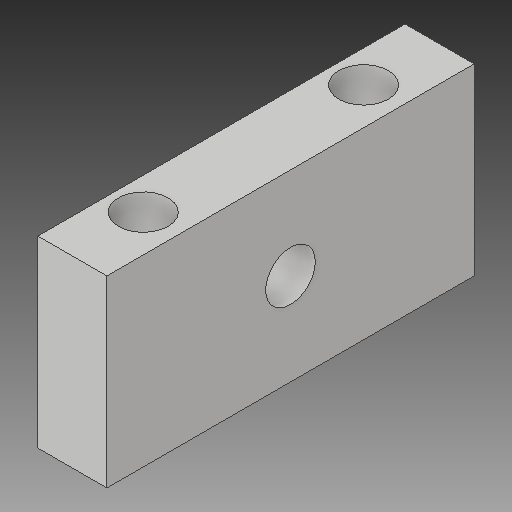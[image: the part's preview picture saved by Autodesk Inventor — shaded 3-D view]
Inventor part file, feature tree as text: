
AUTODESK INVENTOR PART (.ipt)
format: ipt  version: 2017 (Build 210142000, 142)  size: 112,128 bytes
history: native  units: in
note: dims shown in document units (in); Inventor stores cm internally (conversion verified against a paired STEP export)
features: sketch x3, hole x2, other x1, extrude x1
ambient origin geometry x8: Origin, YZ Plane, XZ Plane, XY Plane, X Axis, Y Axis, Z Axis, Center Point
bodies: Solid1 (feature_tree)
feature tree (7):
  other  "WheelIntakeSpringStop"
  extrude  "Extrusion1"  Depth=1.0in
  hole  "Hole1"  [1 undecoded]
  hole  "Hole2"  [1 undecoded]
  sketch  "Sketch1"  dims[d0=0.5in d1=1.0in]
  sketch  "Sketch2"  dims[d2=0.188in d3=0.0in]
  sketch  "Sketch3"  dims[d4=0.135in d5=0.2in d6=0.375in d7=0.25in d8=0.5635in d9=0.25in d10=0.8108in d11=0.5in d12=1.0in d13=0.25in d14=0.5in d15=0.135in d16=0.276in d17=0.375in d18=0.25in d19=0.5635in d20=0.432in d21=0.8108in d22=0.2in d23=0.2in]
note: 2 required parameter values undecoded (feature->parameter linkage not recoverable at this tier; creation-order binding heuristic only, values carry confidence <= 0.55)
